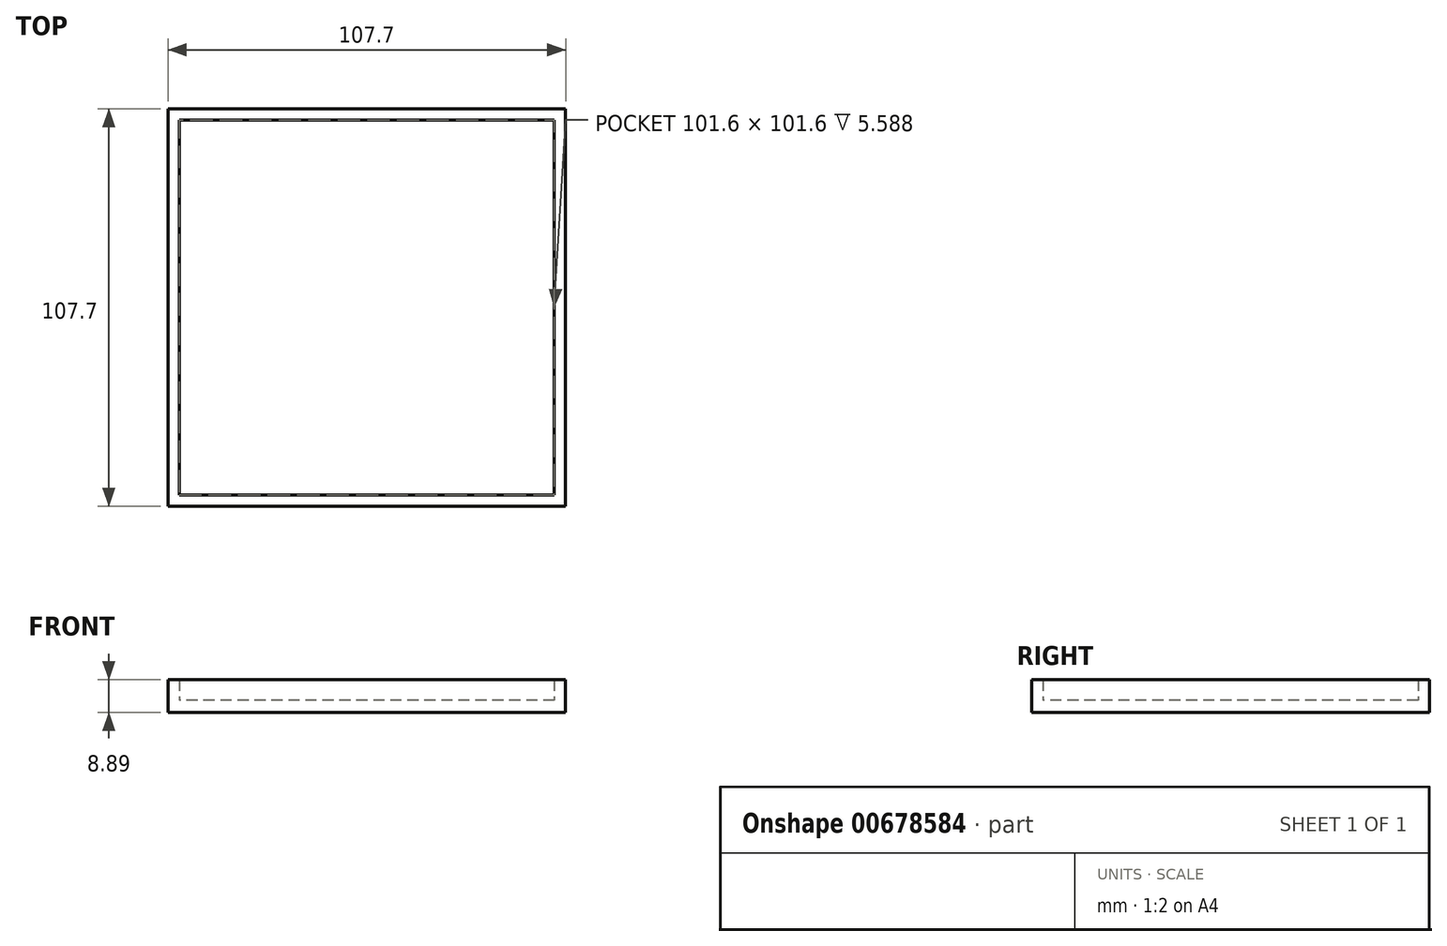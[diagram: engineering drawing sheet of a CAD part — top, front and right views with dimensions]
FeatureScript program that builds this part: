
annotation { "Feature Type Name" : "Feature", "Feature Type Description" : "" }
export const myFeature = defineFeature(function(context is Context, id is Id, definition is map)
    precondition{}
    {
        {
            var Q0;
            Q0=qCreatedBy(makeId("Top.planeOp"),FACE);
            var sketch = newSketch(context, id + "F0", { "sketchPlane" : qUnion([Q0])});
            skLineSegment(sketch, "E0.bottom", {"start": v(50.8, 50.8) * mm, "end": v(-50.8, 50.8) * mm});
            skLineSegment(sketch, "E0.top", {"start": v(50.8, -50.8) * mm, "end": v(-50.8, -50.8) * mm});
            skLineSegment(sketch, "E0.left", {"start": v(50.8, 50.8) * mm, "end": v(50.8, -50.8) * mm});
            skLineSegment(sketch, "E0.right", {"start": v(-50.8, 50.8) * mm, "end": v(-50.8, -50.8) * mm});
            skPoint(sketch, "E0.middle", {"position": v(0, 0) * mm});
            skSolve(sketch);
        }
        {
            var Q0;
            Q0=makeQuery(id+"F0.imprint","IMPRINT",FACE,{"disambiguationData":[TD([[makeQuery(id+"F0.imprint","IMPRINT",EDGE,{"derivedFrom":sQuery(id+"F0.wireOp",EDGE,"E0.bottom")}),1.0]])]});
            var sketch = newSketch(context, id + "F1", { "sketchPlane" : qUnion([Q0])});
            skLineSegment(sketch, "E1.0", {"start": v(-53.85, -53.85) * mm, "end": v(53.85, -53.85) * mm});
            skLineSegment(sketch, "E1.1", {"start": v(-53.85, 53.85) * mm, "end": v(-53.85, -53.85) * mm});
            skLineSegment(sketch, "E1.2", {"start": v(53.85, 53.85) * mm, "end": v(-53.85, 53.85) * mm});
            skLineSegment(sketch, "E1.3", {"start": v(53.85, -53.85) * mm, "end": v(53.85, 53.85) * mm});
            skSolve(sketch);
        }
        {
            var Q0;
            Q0=makeQuery(id+"F1.imprint","IMPRINT",FACE,{"disambiguationData":[TD([[makeQuery(id+"F1.imprint","IMPRINT",EDGE,{"derivedFrom":sQuery(id+"F1.wireOp",EDGE,"E1.0")}),1.0]])]});
            extrude(context, id + "F2", {"entities" : qUnion([Q0]), "depth" : 3.8 * mm, "offsetDistance" : 25.4 * mm});
        }
        {
            var Q0;
            Q0=makeQuery(id+"F0.imprint","IMPRINT",FACE,{"disambiguationData":[TD([[makeQuery(id+"F0.imprint","IMPRINT",EDGE,{"derivedFrom":sQuery(id+"F0.wireOp",EDGE,"E0.bottom")}),1.0]])]});
            extrude(context, id + "F3", {"entities" : qUnion([Q0]), "operationType" : NewBodyOperationType.ADD, "depth" : 3.3 * mm, "offsetDistance" : 25.4 * mm});
        }
        {
            var Q0;
            Q0=makeQuery(id+"F2.opExtrude","CAP_FACE",FACE,{"disambiguationData":[OSD([sQuery(id+"F0.wireOp",EDGE,"E0.bottom"),sQuery(id+"F0.wireOp",EDGE,"E0.top"),sQuery(id+"F0.wireOp",EDGE,"E0.left"),sQuery(id+"F0.wireOp",EDGE,"E0.right"),sQuery(id+"F1.wireOp",EDGE,"E1.0"),sQuery(id+"F1.wireOp",EDGE,"E1.1"),sQuery(id+"F1.wireOp",EDGE,"E1.2"),sQuery(id+"F1.wireOp",EDGE,"E1.3")])],"isStart":false});
            extrude(context, id + "F4", {"entities" : qUnion([Q0]), "operationType" : NewBodyOperationType.ADD, "depth" : 5.08 * mm, "offsetDistance" : 25.4 * mm});
        }
    });
